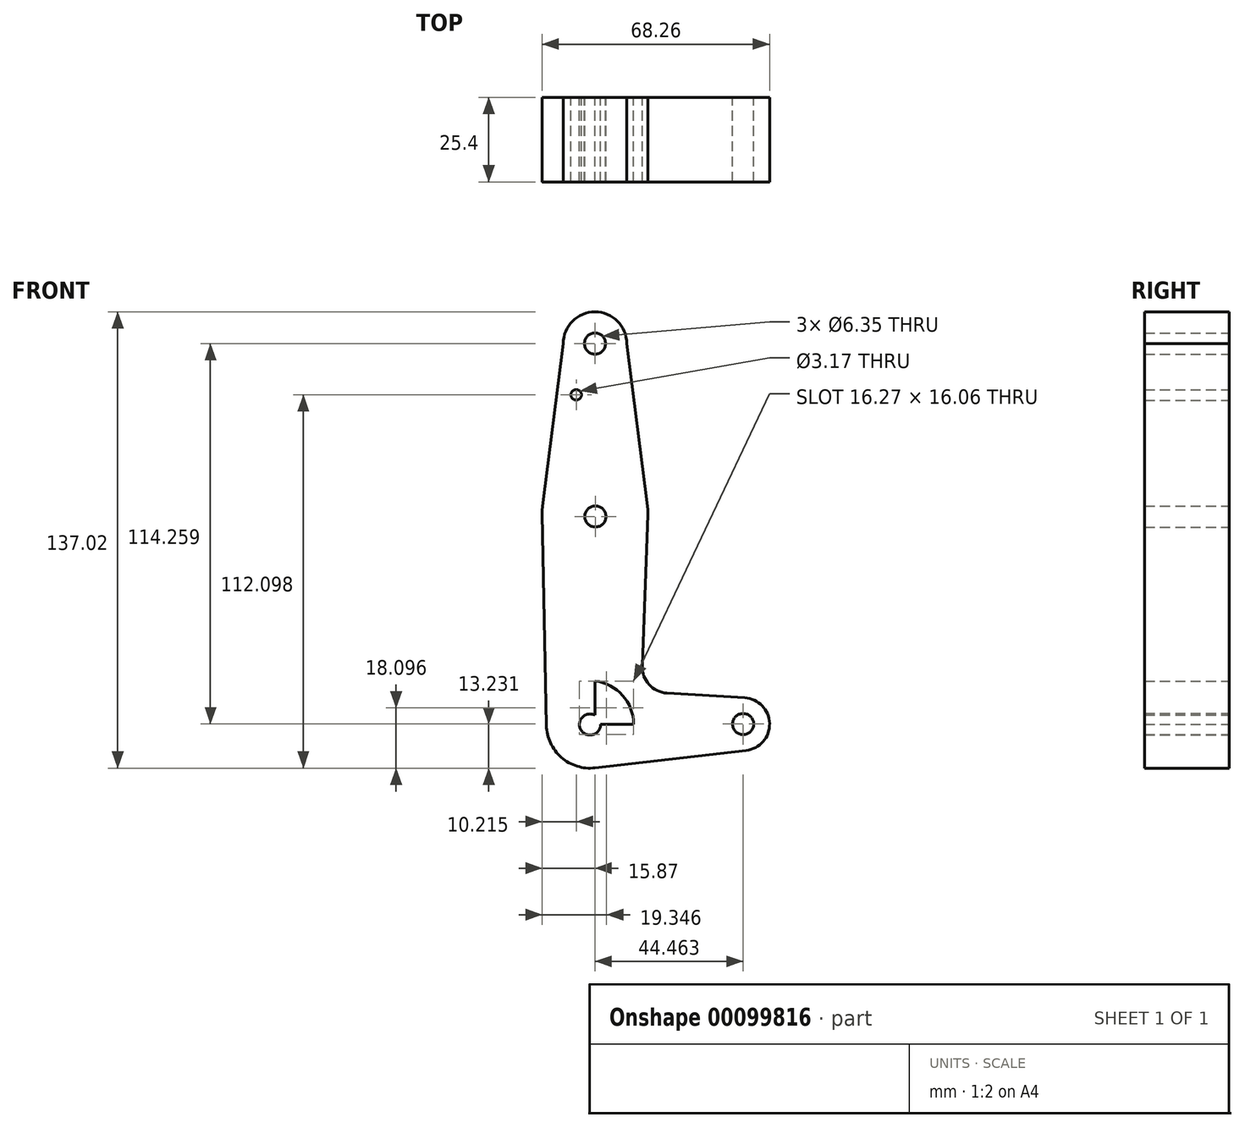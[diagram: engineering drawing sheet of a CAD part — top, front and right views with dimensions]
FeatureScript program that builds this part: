
annotation { "Feature Type Name" : "Feature", "Feature Type Description" : "" }
export const myFeature = defineFeature(function(context is Context, id is Id, definition is map)
    precondition{}
    {
        {
            var Q0;
            Q0=qCreatedBy(makeId("Front.planeOp"),FACE);
            var sketch = newSketch(context, id + "F0", { "sketchPlane" : qUnion([Q0])});
            skLineSegment(sketch, "E0", {"start": v(0, 114.3) * mm, "end": v(0, 0) * mm});
            skLineSegment(sketch, "E1", {"start": v(0, 0) * mm, "end": v(44.45, 0) * mm});
            skCircle(sketch, "E2", {"center": v(0, 114.3) * mm, "radius": 9.53 * mm});
            skCircle(sketch, "E3", {"center": v(0, 63.5) * mm, "radius": 15.88 * mm});
            skCircle(sketch, "E4", {"center": v(44.45, 0) * mm, "radius": 7.94 * mm});
            skLineSegment(sketch, "E5", {"start": v(9.52, 114.3) * mm, "end": v(15.75, 65.5) * mm});
            skLineSegment(sketch, "E6", {"start": v(-9.53, 114.3) * mm, "end": v(-15.75, 65.5) * mm});
            skLineSegment(sketch, "E7", {"start": v(15.86, 62.9) * mm, "end": v(14.17, 17.57) * mm});
            skLineSegment(sketch, "E8", {"start": v(21.63, 9.34) * mm, "end": v(44.93, 7.92) * mm});
            skArc(sketch, "E9.filletArc", {"start": v(14.17, 17.57) * mm, "mid": v(16.22, 11.94) * mm, "end": v(21.63, 9.34) * mm});
            skCircle(sketch, "E10", {"center": v(0, 114.3) * mm, "radius": 3.18 * mm});
            skCircle(sketch, "E11", {"center": v(0.1, 62.38) * mm, "radius": 3.18 * mm});
            skCircle(sketch, "E12", {"center": v(-1.5, -0.08) * mm, "radius": 3.18 * mm});
            skCircle(sketch, "E13", {"center": v(44.46, 0.04) * mm, "radius": 3.18 * mm});
            skCircle(sketch, "E14", {"center": v(-5.65, 98.9) * mm, "radius": 1.59 * mm});
            skLineSegment(sketch, "E15", {"start": v(-15.87, 63.18) * mm, "end": v(-14.6, -0.59) * mm});
            skCircle(sketch, "E16", {"center": v(-1.5, -0.08) * mm, "radius": 13.1 * mm});
            skLineSegment(sketch, "E17", {"start": v(0, -13.1) * mm, "end": v(45.36, -7.89) * mm});
            skSolve(sketch);
        }
        {
            var Q0;
            Q0 = qSketchRegion(id + "F0", true);
            extrude(context, id + "F1", {"entities" : qUnion([Q0]), "depth" : 25.4 * mm});
        }
    });
